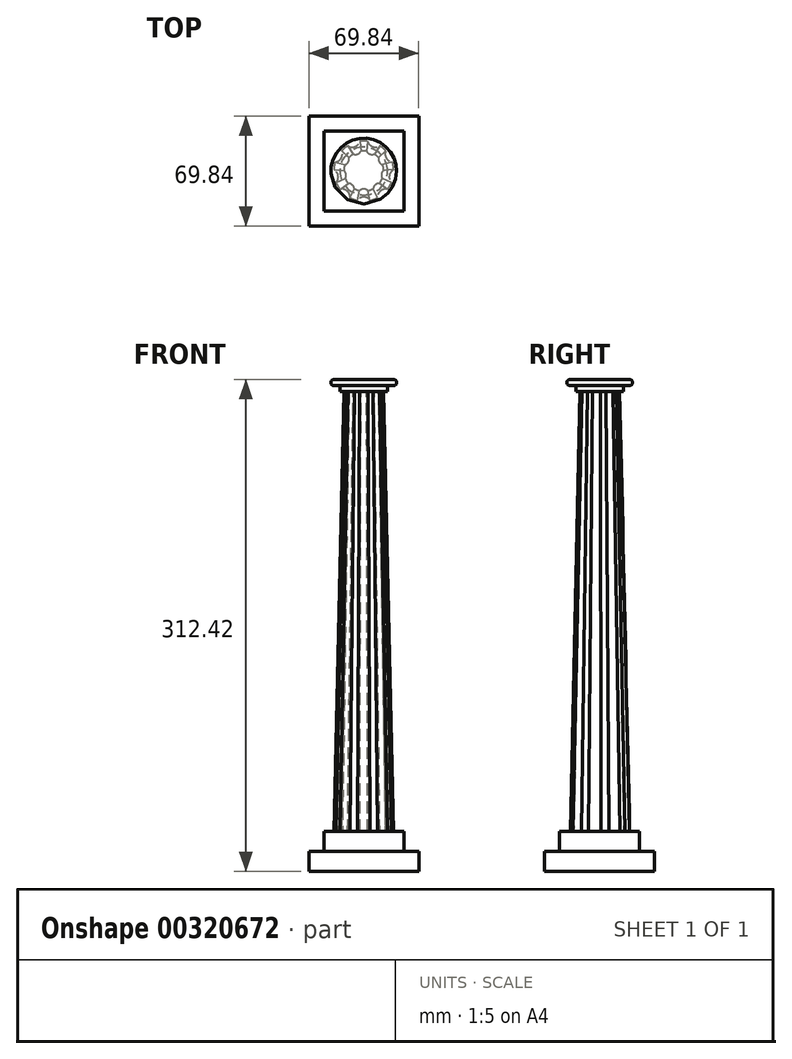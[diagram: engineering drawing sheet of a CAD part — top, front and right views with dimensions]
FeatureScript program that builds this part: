
annotation { "Feature Type Name" : "Feature", "Feature Type Description" : "" }
export const myFeature = defineFeature(function(context is Context, id is Id, definition is map)
    precondition{}
    {
        {
            var Q0;
            Q0=qCreatedBy(makeId("Top.planeOp"),FACE);
            var sketch = newSketch(context, id + "F0", { "sketchPlane" : qUnion([Q0])});
            skLineSegment(sketch, "E0.bottom", {"start": v(-34.92, 34.93) * mm, "end": v(34.93, 34.93) * mm});
            skLineSegment(sketch, "E0.top", {"start": v(-34.93, -34.93) * mm, "end": v(34.92, -34.93) * mm});
            skLineSegment(sketch, "E0.left", {"start": v(-34.92, 34.93) * mm, "end": v(-34.93, -34.93) * mm});
            skLineSegment(sketch, "E0.right", {"start": v(34.93, 34.93) * mm, "end": v(34.92, -34.93) * mm});
            skPoint(sketch, "E0.middle", {"position": v(0, 0) * mm});
            skSolve(sketch);
        }
        {
            var Q0;
            Q0=makeQuery(id+"F0.imprint","IMPRINT",FACE,{"disambiguationData":[TD([[makeQuery(id+"F0.imprint","IMPRINT",EDGE,{"derivedFrom":sQuery(id+"F0.wireOp",EDGE,"E0.bottom")}),-1.0]])]});
            extrude(context, id + "F1", {"entities" : qUnion([Q0]), "depth" : 12.7 * mm});
        }
        {
            var Q0;
            Q0=makeQuery(id+"F1.opExtrude","CAP_FACE",FACE,{"disambiguationData":[OSD([sQuery(id+"F0.wireOp",EDGE,"E0.bottom"),sQuery(id+"F0.wireOp",EDGE,"E0.top"),sQuery(id+"F0.wireOp",EDGE,"E0.left"),sQuery(id+"F0.wireOp",EDGE,"E0.right")])],"isStart":false});
            var sketch = newSketch(context, id + "F2", { "sketchPlane" : qUnion([Q0])});
            skLineSegment(sketch, "E1.bottom", {"start": v(-25.4, 25.4) * mm, "end": v(25.4, 25.4) * mm});
            skLineSegment(sketch, "E1.top", {"start": v(-25.4, -25.4) * mm, "end": v(25.4, -25.4) * mm});
            skLineSegment(sketch, "E1.left", {"start": v(-25.4, 25.4) * mm, "end": v(-25.4, -25.4) * mm});
            skLineSegment(sketch, "E1.right", {"start": v(25.4, 25.4) * mm, "end": v(25.4, -25.4) * mm});
            skPoint(sketch, "E1.middle", {"position": v(0, 0) * mm});
            skSolve(sketch);
        }
        {
            var Q0;
            Q0=makeQuery(id+"F2.imprint","IMPRINT",FACE,{"disambiguationData":[TD([[makeQuery(id+"F2.imprint","IMPRINT",EDGE,{"derivedFrom":sQuery(id+"F2.wireOp",EDGE,"E1.bottom")}),-1.0]])]});
            extrude(context, id + "F3", {"entities" : qUnion([Q0]), "operationType" : NewBodyOperationType.ADD, "depth" : 12.7 * mm});
        }
        {
            var Q0;
            Q0=makeQuery(id+"F3.opExtrude","CAP_FACE",FACE,{"disambiguationData":[OSD([sQuery(id+"F2.wireOp",EDGE,"E1.bottom"),sQuery(id+"F2.wireOp",EDGE,"E1.top"),sQuery(id+"F2.wireOp",EDGE,"E1.left"),sQuery(id+"F2.wireOp",EDGE,"E1.right")])],"isStart":false});
            var sketch = newSketch(context, id + "F4", { "sketchPlane" : qUnion([Q0])});
            skCircle(sketch, "E2", {"center": v(0, 0) * mm, "radius": 19.05 * mm});
            skArc(sketch, "E3", {"start": v(4.1, -18.6) * mm, "mid": v(0, -16.51) * mm, "end": v(-4.1, -18.6) * mm});
            skArc(sketch, "E4.1.0", {"start": v(15.1, -11.6) * mm, "mid": v(10.61, -12.65) * mm, "end": v(8.8, -16.9) * mm});
            skArc(sketch, "E4.2.0", {"start": v(19.03, 0.82) * mm, "mid": v(16.26, -2.87) * mm, "end": v(17.6, -7.28) * mm});
            skArc(sketch, "E4.3.0", {"start": v(14.06, 12.86) * mm, "mid": v(14.3, 8.25) * mm, "end": v(18.16, 5.74) * mm});
            skArc(sketch, "E4.4.0", {"start": v(2.5, 18.89) * mm, "mid": v(5.65, 15.51) * mm, "end": v(10.22, 16.07) * mm});
            skArc(sketch, "E4.5.0", {"start": v(-10.22, 16.07) * mm, "mid": v(-5.65, 15.51) * mm, "end": v(-2.5, 18.89) * mm});
            skArc(sketch, "E4.6.0", {"start": v(-18.16, 5.74) * mm, "mid": v(-14.3, 8.26) * mm, "end": v(-14.06, 12.86) * mm});
            skArc(sketch, "E4.7.0", {"start": v(-17.6, -7.28) * mm, "mid": v(-16.26, -2.87) * mm, "end": v(-19.03, 0.82) * mm});
            skArc(sketch, "E4.8.0", {"start": v(-8.8, -16.9) * mm, "mid": v(-10.61, -12.65) * mm, "end": v(-15.1, -11.6) * mm});
            skSolve(sketch);
        }
        {
            var Q0;
            Q0=qCreatedBy(makeId("Top.planeOp"),FACE);
            cPlane(context, id + "F5", {"entities" : qUnion([Q0]), "cplaneType" : CPlaneType.OFFSET, "offset" : 304.8 * mm, "width" : 152.4 * mm, "height" : 152.4 * mm});
        }
        {
            var Q0;
            Q0=qCreatedBy(id+"F5.planeOp",FACE);
            var sketch = newSketch(context, id + "F6", { "sketchPlane" : qUnion([Q0])});
            skCircle(sketch, "E5", {"center": v(0, 0) * mm, "radius": 12.7 * mm});
            skArc(sketch, "E6", {"start": v(2.58, -12.44) * mm, "mid": v(0, -11.43) * mm, "end": v(-2.58, -12.44) * mm});
            skArc(sketch, "E7.1.0", {"start": v(9.97, -7.87) * mm, "mid": v(7.35, -8.76) * mm, "end": v(6.02, -11.18) * mm});
            skArc(sketch, "E7.2.0", {"start": v(12.7, 0.38) * mm, "mid": v(11.26, -1.98) * mm, "end": v(11.8, -4.7) * mm});
            skArc(sketch, "E7.3.0", {"start": v(9.48, 8.45) * mm, "mid": v(9.9, 5.71) * mm, "end": v(12.06, 3.98) * mm});
            skArc(sketch, "E7.4.0", {"start": v(1.83, 12.57) * mm, "mid": v(3.9, 10.74) * mm, "end": v(6.68, 10.8) * mm});
            skArc(sketch, "E7.5.0", {"start": v(-6.68, 10.8) * mm, "mid": v(-3.9, 10.74) * mm, "end": v(-1.83, 12.57) * mm});
            skArc(sketch, "E7.6.0", {"start": v(-12.06, 3.98) * mm, "mid": v(-9.9, 5.72) * mm, "end": v(-9.48, 8.45) * mm});
            skArc(sketch, "E7.7.0", {"start": v(-11.8, -4.7) * mm, "mid": v(-11.26, -1.98) * mm, "end": v(-12.7, 0.38) * mm});
            skArc(sketch, "E7.8.0", {"start": v(-6.02, -11.18) * mm, "mid": v(-7.35, -8.76) * mm, "end": v(-9.97, -7.87) * mm});
            skSolve(sketch);
        }
        {
            var Q1;
            {var subQ0=sQuery(id+"F4.wireOp",EDGE,"E3");Q1=makeQuery(id+"F4.imprint","IMPRINT",FACE,{"disambiguationData":[TD([[makeQuery(id+"F4.imprint","IMPRINT",EDGE,{"derivedFrom":subQ0}),-1.0]])]});}
            var Q2;
            {var subQ0=sQuery(id+"F6.wireOp",EDGE,"E6");Q2=makeQuery(id+"F6.imprint","IMPRINT",FACE,{"disambiguationData":[TD([[makeQuery(id+"F6.imprint","IMPRINT",EDGE,{"derivedFrom":subQ0}),-1.0]])]});}
            loft(context, id + "F7", {"operationType" : NewBodyOperationType.ADD, "sheetProfilesArray" : [{ "sheetProfileEntities" : qUnion([Q1]) }, { "sheetProfileEntities" : qUnion([Q2]) }]});
        }
        {
            var Q0;
            {var subQ0=sQuery(id+"F6.wireOp",EDGE,"E6");Q0=makeQuery(id+"F7.opLoft","CAP_FACE",FACE,{"disambiguationData":[OSD([makeQuery(id+"F6.imprint","IMPRINT",FACE,{"disambiguationData":[TD([[makeQuery(id+"F6.imprint","IMPRINT",EDGE,{"derivedFrom":subQ0}),-1.0]])]})])],"isStart":true});}
            var sketch = newSketch(context, id + "F8", { "sketchPlane" : qUnion([Q0])});
            skCircle(sketch, "E8", {"center": v(0, 0) * mm, "radius": 15.24 * mm});
            skSolve(sketch);
        }
        {
            var Q0;
            Q0=qCreatedBy(makeId("Front.planeOp"),FACE);
            var sketch = newSketch(context, id + "F9", { "sketchPlane" : qUnion([Q0])});
            skLineSegment(sketch, "E9", {"start": v(0, 190.16) * mm, "end": v(15.24, 190.16) * mm});
            skLineSegment(sketch, "E10", {"start": v(15.16, 304.8) * mm, "end": v(15.16, 308.6) * mm});
            skLineSegment(sketch, "E11", {"start": v(15.16, 308.6) * mm, "end": v(18.97, 308.6) * mm});
            skArc(sketch, "E12", {"start": v(18.97, 308.6) * mm, "mid": v(20.88, 310.51) * mm, "end": v(18.97, 312.42) * mm});
            skLineSegment(sketch, "E13", {"start": v(18.97, 312.42) * mm, "end": v(0, 312.42) * mm});
            skLineSegment(sketch, "E14", {"start": v(0, 312.42) * mm, "end": v(0, 304.8) * mm});
            skLineSegment(sketch, "E15", {"start": v(0, 304.8) * mm, "end": v(15.16, 304.8) * mm});
            skSolve(sketch);
        }
        {
            var Q0;
            Q0=makeQuery(id+"F9.imprint","IMPRINT",FACE,{"disambiguationData":[TD([[makeQuery(id+"F9.imprint","IMPRINT",EDGE,{"derivedFrom":sQuery(id+"F9.wireOp",EDGE,"E10")}),1.0]])]});
            var Q1;
            Q1=sQuery(id+"F9.wireOp",EDGE,"E14");
            revolve(context, id + "F10", {"operationType" : NewBodyOperationType.ADD, "entities" : qUnion([Q0]), "axis" : qUnion([Q1]), "revolveType" : RevolveType.FULL});
        }
    });
